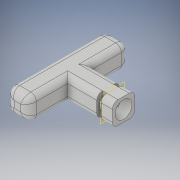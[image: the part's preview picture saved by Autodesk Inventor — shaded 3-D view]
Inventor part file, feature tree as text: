
AUTODESK INVENTOR PART (.ipt)
format: ipt  version: 2019 (Build 230136000, 136)  size: 435,712 bytes
history: native  units: in
note: dims shown in document units (in); Inventor stores cm internally (conversion verified against a paired STEP export)
features: extrude x4, sketch x4, fillet x3, plane x3, other x1
ambient origin geometry x8: Origin, YZ Plane, XZ Plane, XY Plane, X Axis, Y Axis, Z Axis, Center Point
bodies: Body1 (feature_tree)
feature tree (15):
  other  "Sólido1"
  extrude  "Extrusión1"  Depth=0.7874in
  fillet  "Empalme1"  Radius=3.5433in
  fillet  "Empalme2"  Radius=0.1969in
  plane  "Plano de trabajo1"
  extrude  "Extrusión2"  [1 undecoded]
  fillet  "Empalme3"  Radius=0.3937in
  plane  "Plano de trabajo2"
  extrude  "Extrusión3"  Depth=0.7874in
  extrude  "Extrusión4"  Depth=0.1969in
  plane  "Plano de trabajo3"
  sketch  "Boceto1"  dims[d0=0.7874in d1=0.7874in d2=3.5433in d3=0.0in d4=0.1969in]
  sketch  "Boceto2"  dims[d5=0.2756in d6=-0.3937in d7=0.3937in]
  sketch  "Boceto3"  dims[d8=0.7874in d9=0.7874in]
  sketch  "Boceto4"  dims[d10=1.9685in d11=0.0in d12=0.1969in d13=-0.3937in d14=0.3937in d15=0.5984in d16=1.1811in d17=0.0in d19=0.1496in d20=0.0in d21=-0.3937in d28=0.1969in d29=0.1969in d30=1.0907in]
note: 1 required parameter value undecoded (feature->parameter linkage not recoverable at this tier; creation-order binding heuristic only, values carry confidence <= 0.55)
